# Revit family: KS Husky, Typ VI-32, M10-M12, Ø 60,3- 88,9
name_source: partatom
category: HLS-Bauteile
revit_build: Autodesk Revit 2017 (Build: 20190507_1515(x64)
units: mm (PartAtom-declared; Revit-internal decimal feet)

## family parameters
Arbeitsebenenbasiert = Ja
Beim Laden mit Abzugskörper schneiden = Nein
Bemaßung runder Anschluss = Durchmesser verwenden
Gemeinsam genutzt = Ja
Immer vertikal = Nein
Raumberechnungspunkt = Nein
Teiletyp = Normal

## types (3) — shared parameters
Anschluss = M10/M12
Baustoffklasse = B2
DVS = 5 mm  [stored 0.0164042 ft]
Dichte Kern = 120 kg/m³
Dämmkörper = KA/PU
Fabrikat = MEFA
Firma = MEFA Befestigungs- und Montagesysteme GmbH
H1 = 2 mm  [stored 0.00656168 ft]
H2 = 4 mm  [stored 0.0131234 ft]
HGA = 22 mm  [stored 0.0721785 ft]
Kurztext1 = Kälteschelle Husky VI 32
L = 51 mm
MB = 25 mm  [stored 0.082021 ft]
MD = 3 mm  [stored 0.00984252 ft]
Material = Stahl
Material Mantel = Kunststoff
Materialname = DD11
Mengeneinheit = St
Oberflaeche = galvanisch verzinkt
Rohrschellentyp = Trabant
Schalenlänge = 42 mm
Typ = VI 32
Vorgabe-Ansicht = 1219 mm
Wasserdampfdiffusionswiderstand = 7000 µ
Wärmeleitfähigkeit = 0.029 W/mK
max. Temperaturbeständigkeit = 105 °C
mittl. Nenndruckfestigkeit Kern = 1,35 N/mm²
stat. Belastung Kern = 0,27 N/mm²
vpe = 8 St

## per-type parameters (varying)
| type | A | Anschlußhöhe | Artikelnummer | B | Breite | D | D0 | DF1 | DF2 | DS | Dämmstärke | EAN | Gewicht | Gewicht pro Bauteil | H | Kurztext2 | R | RM | Rohraußendurchmesser Stahl | S | max. zul. Last |
| Kälteschelle Husky, Typ VI-32, M10/M12, Ø 60,3 | 59 mm | 57 mm | 6850601 | 177 mm | 176 mm  [stored 0.577428 ft] | 60 mm | 130 mm | 21 mm  [stored 0.0688976 ft] | 21 mm  [stored 0.0688976 ft] | 35 mm  [stored 0.114829 ft] | 35 mm  [stored 0.114829 ft] | 4250928441034 | 0.35 kg | 0.35 kg | 157 mm | 60,3 mm Iso 35 x 42 mm M10/M12 | 65 mm | 68 mm | 60,3 mm | 156 mm | 0.60 kN |
| Kälteschelle Husky, Typ VI-32, M10/M12, Ø 76,1 | 61 mm  [stored 0.200131 ft] | 62 mm | 6850761 | 193 mm | 192 mm  [stored 0.629921 ft] | 76 mm | 149 mm | 20 mm  [stored 0.0656168 ft] | 19 mm  [stored 0.062336 ft] | 37 mm  [stored 0.121391 ft] | 37 mm  [stored 0.121391 ft] | 4250928441041 | 0.39 kg | 0.39 kg | 176 mm  [stored 0.577428 ft] | 76,1 mm Iso 37 x 42 mm M10/M12 | 75 mm | 77 mm | 76,1 mm | 173 mm  [stored 0.567585 ft] | 0.75 kN |
| Kälteschelle Husky, Typ VI-32, M10/M12, Ø 88,9 | 65 mm | 64 mm | 6850891 | 215 mm | 215 mm | 89 mm | 169 mm | 21 mm  [stored 0.0688976 ft] | 20 mm  [stored 0.0656168 ft] | 40 mm  [stored 0.131234 ft] | 40 mm  [stored 0.131234 ft] | 4250928441058 | 0.44 kg | 0.44 kg | 196 mm | 88,9 mm Iso 40 x 42 mm M10/M12 | 85 mm | 87 mm | 88,9 mm | 194 mm | 0.88 kN |

note: [stored X ft] marks values corroborated as IEEE doubles in the binary element streams (Revit-internal decimal feet)

## geometry (parser evidence)
native form markers: Sweep x3
no freeform markers — native parametric forms only
